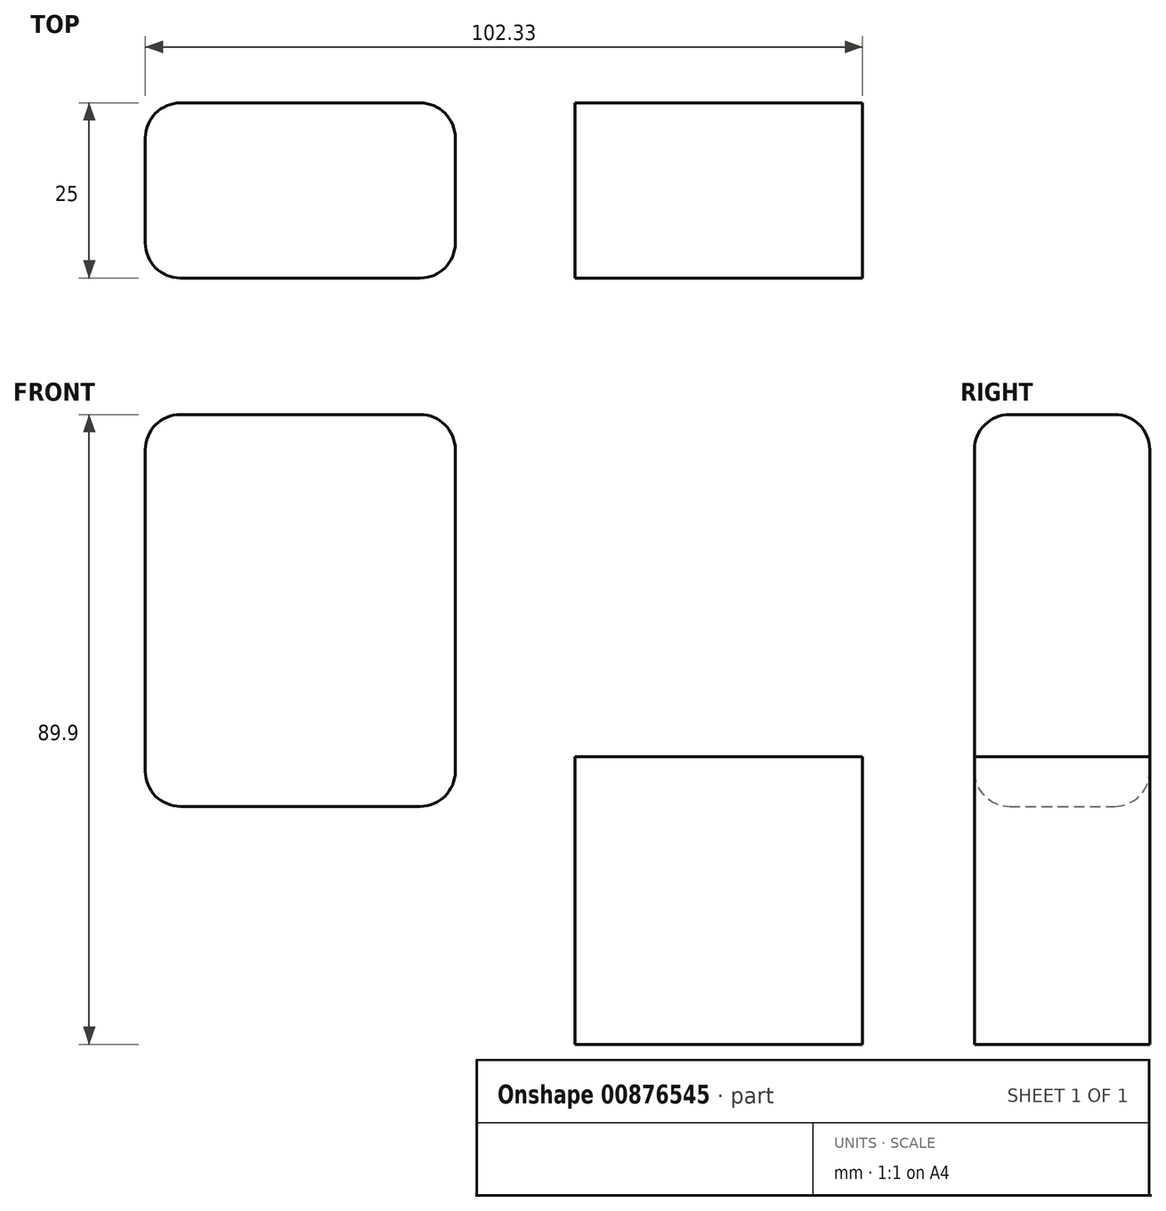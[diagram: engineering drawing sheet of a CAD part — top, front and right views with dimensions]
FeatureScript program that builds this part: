
annotation { "Feature Type Name" : "Feature", "Feature Type Description" : "" }
export const myFeature = defineFeature(function(context is Context, id is Id, definition is map)
    precondition{}
    {
        {
            var Q0;
            Q0=qCreatedBy(makeId("Front.planeOp"),FACE);
            var sketch = newSketch(context, id + "F0", { "sketchPlane" : qUnion([Q0])});
            skLineSegment(sketch, "E0.bottom", {"start": v(-191.22, 55.93) * mm, "end": v(-147, 55.93) * mm});
            skLineSegment(sketch, "E0.top", {"start": v(-191.22, 0) * mm, "end": v(-147, 0) * mm});
            skLineSegment(sketch, "E0.left", {"start": v(-191.22, 55.93) * mm, "end": v(-191.22, 0) * mm});
            skLineSegment(sketch, "E0.right", {"start": v(-147, 55.93) * mm, "end": v(-147, 0) * mm});
            skLineSegment(sketch, "E1.bottom", {"start": v(-129.94, 7.08) * mm, "end": v(-88.89, 7.08) * mm});
            skLineSegment(sketch, "E1.top", {"start": v(-129.94, -33.97) * mm, "end": v(-88.89, -33.97) * mm});
            skLineSegment(sketch, "E1.left", {"start": v(-129.94, 7.08) * mm, "end": v(-129.94, -33.97) * mm});
            skLineSegment(sketch, "E1.right", {"start": v(-88.89, 7.08) * mm, "end": v(-88.89, -33.97) * mm});
            skSolve(sketch);
        }
        {
            var Q0;
            Q0=makeQuery(id+"F0.imprint","IMPRINT",FACE,{"disambiguationData":[TD([[makeQuery(id+"F0.imprint","IMPRINT",EDGE,{"derivedFrom":sQuery(id+"F0.wireOp",EDGE,"E0.bottom")}),-1.0]])]});
            var Q1;
            Q1=makeQuery(id+"F0.imprint","IMPRINT",FACE,{"disambiguationData":[TD([[makeQuery(id+"F0.imprint","IMPRINT",EDGE,{"derivedFrom":sQuery(id+"F0.wireOp",EDGE,"E1.bottom")}),-1.0]])]});
            extrude(context, id + "F1", {"entities" : qUnion([Q0, Q1]), "depth" : 25 * mm, "offsetDistance" : 25 * mm});
        }
        {
            var Q0;
            Q0=makeQuery(id+"F1.opExtrude","CAP_FACE",FACE,{"disambiguationData":[OSD([sQuery(id+"F0.wireOp",EDGE,"E0.bottom"),sQuery(id+"F0.wireOp",EDGE,"E0.top"),sQuery(id+"F0.wireOp",EDGE,"E0.left"),sQuery(id+"F0.wireOp",EDGE,"E0.right")])],"isStart":false});
            var Q1;
            Q1=makeQuery(id+"F1.opExtrude","CAP_FACE",FACE,{"disambiguationData":[OSD([sQuery(id+"F0.wireOp",EDGE,"E0.bottom"),sQuery(id+"F0.wireOp",EDGE,"E0.top"),sQuery(id+"F0.wireOp",EDGE,"E0.left"),sQuery(id+"F0.wireOp",EDGE,"E0.right")])],"isStart":true});
            var Q2;
            Q2=makeQuery(id+"F1.opExtrude","SWEPT_FACE",FACE,{"disambiguationData":[OSD([sQuery(id+"F0.wireOp",EDGE,"E0.bottom")])]});
            var Q3;
            Q3=makeQuery(id+"F1.opExtrude","SWEPT_FACE",FACE,{"disambiguationData":[OSD([sQuery(id+"F0.wireOp",EDGE,"E0.top")])]});
            fillet(context, id + "F2", {"entities" : qUnion([Q0, Q1, Q2, Q3]), "radius" : 5 * mm, "tangentPropagation" : true, "allowEdgeOverflow" : false});
        }
    });
